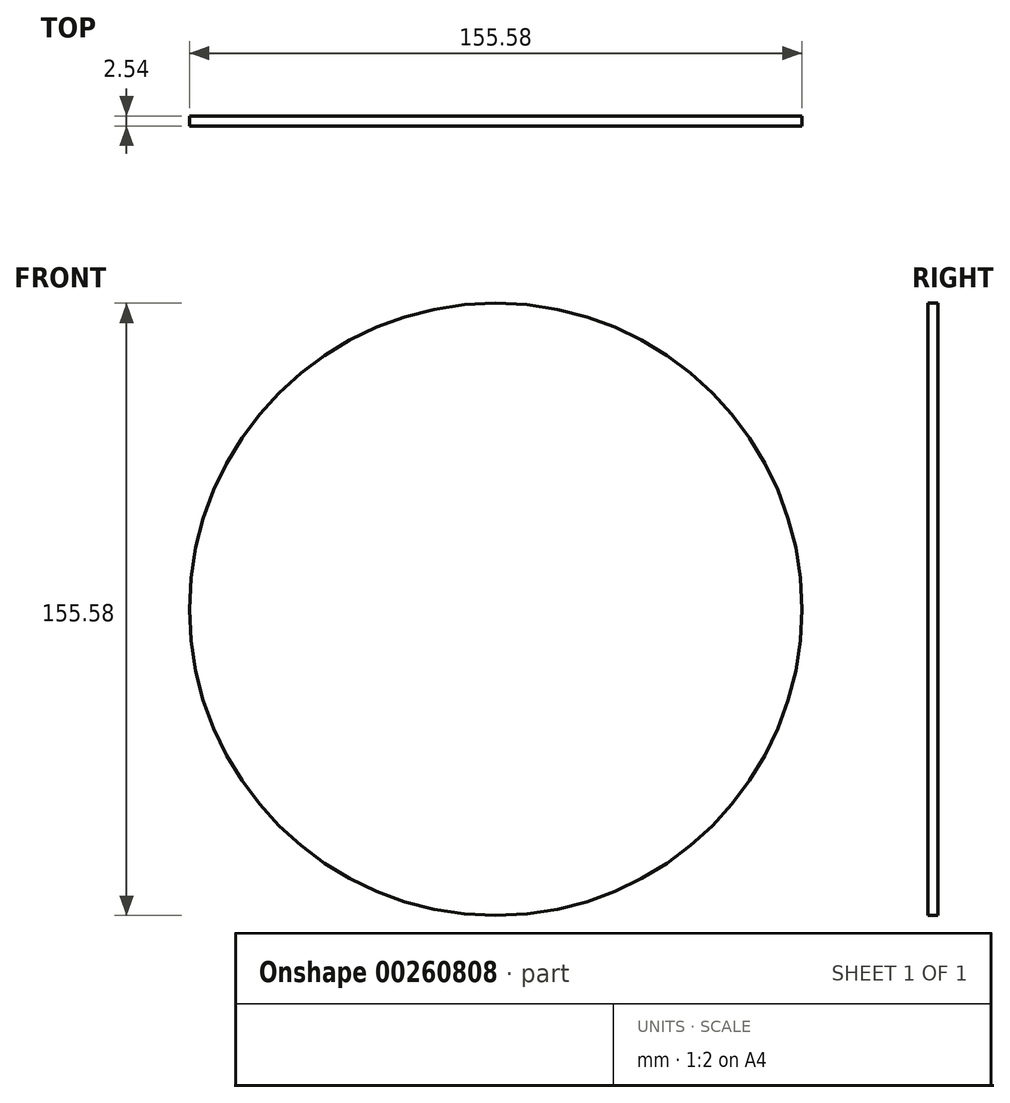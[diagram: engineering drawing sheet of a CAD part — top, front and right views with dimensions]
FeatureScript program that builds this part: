
annotation { "Feature Type Name" : "Feature", "Feature Type Description" : "" }
export const myFeature = defineFeature(function(context is Context, id is Id, definition is map)
    precondition{}
    {
        {
            var Q0;
            Q0=qCreatedBy(makeId("Front.planeOp"),FACE);
            var sketch = newSketch(context, id + "F0", { "sketchPlane" : qUnion([Q0])});
            skCircle(sketch, "E0", {"center": v(0, 0) * mm, "radius": 68.26 * mm});
            skCircle(sketch, "E1", {"center": v(0, 0) * mm, "radius": 77.79 * mm});
            skLineSegment(sketch, "E2.bottom", {"start": v(4.76, 77.64) * mm, "end": v(-4.76, 77.64) * mm});
            skLineSegment(sketch, "E2.top", {"start": v(4.76, -77.64) * mm, "end": v(-4.76, -77.64) * mm});
            skLineSegment(sketch, "E2.left", {"start": v(4.76, 77.64) * mm, "end": v(4.76, -77.64) * mm});
            skLineSegment(sketch, "E2.right", {"start": v(-4.76, 77.64) * mm, "end": v(-4.76, -77.64) * mm});
            skSolve(sketch);
        }
        {
            var Q0;
            Q0 = qSketchRegion(id + "F0", true);
            var Q1;
            {var subQ0=sQuery(id+"F0.wireOp",EDGE,"E2.right");var subQ1=sQuery(id+"F0.wireOp",EDGE,"E0");var subQ2=makeQuery(id+"F0.imprint","INTERSECT",VERTEX,{"disambiguationData":[OD(0.0)],"derivedFrom":[subQ1,subQ0]});Q1=makeQuery(id+"F0.imprint","IMPRINT",FACE,{"disambiguationData":[TD([[makeQuery(id+"F0.imprint","IMPRINT",EDGE,{"disambiguationData":[TD([[subQ2,-1.0]])],"derivedFrom":subQ1}),1.0]])]});}
            var Q2;
            {var subQ0=sQuery(id+"F0.wireOp",EDGE,"E2.left");var subQ1=sQuery(id+"F0.wireOp",EDGE,"E0");var subQ2=makeQuery(id+"F0.imprint","INTERSECT",VERTEX,{"disambiguationData":[OD(0.0)],"derivedFrom":[subQ1,subQ0]});Q2=makeQuery(id+"F0.imprint","IMPRINT",FACE,{"disambiguationData":[TD([[makeQuery(id+"F0.imprint","IMPRINT",EDGE,{"disambiguationData":[TD([[subQ2,1.0]])],"derivedFrom":subQ1}),1.0]])]});}
            var Q3;
            {var subQ0=sQuery(id+"F0.wireOp",EDGE,"E2.right");var subQ1=sQuery(id+"F0.wireOp",EDGE,"E0");var subQ2=makeQuery(id+"F0.imprint","INTERSECT",VERTEX,{"disambiguationData":[OD(0.0)],"derivedFrom":[subQ1,subQ0]});Q3=makeQuery(id+"F0.imprint","IMPRINT",FACE,{"disambiguationData":[TD([[makeQuery(id+"F0.imprint","IMPRINT",EDGE,{"disambiguationData":[TD([[subQ2,1.0]])],"derivedFrom":subQ1}),1.0]])]});}
            extrude(context, id + "F1", {"entities" : qUnion([Q0, Q1, Q2, Q3]), "depth" : 2.54 * mm});
        }
    });
